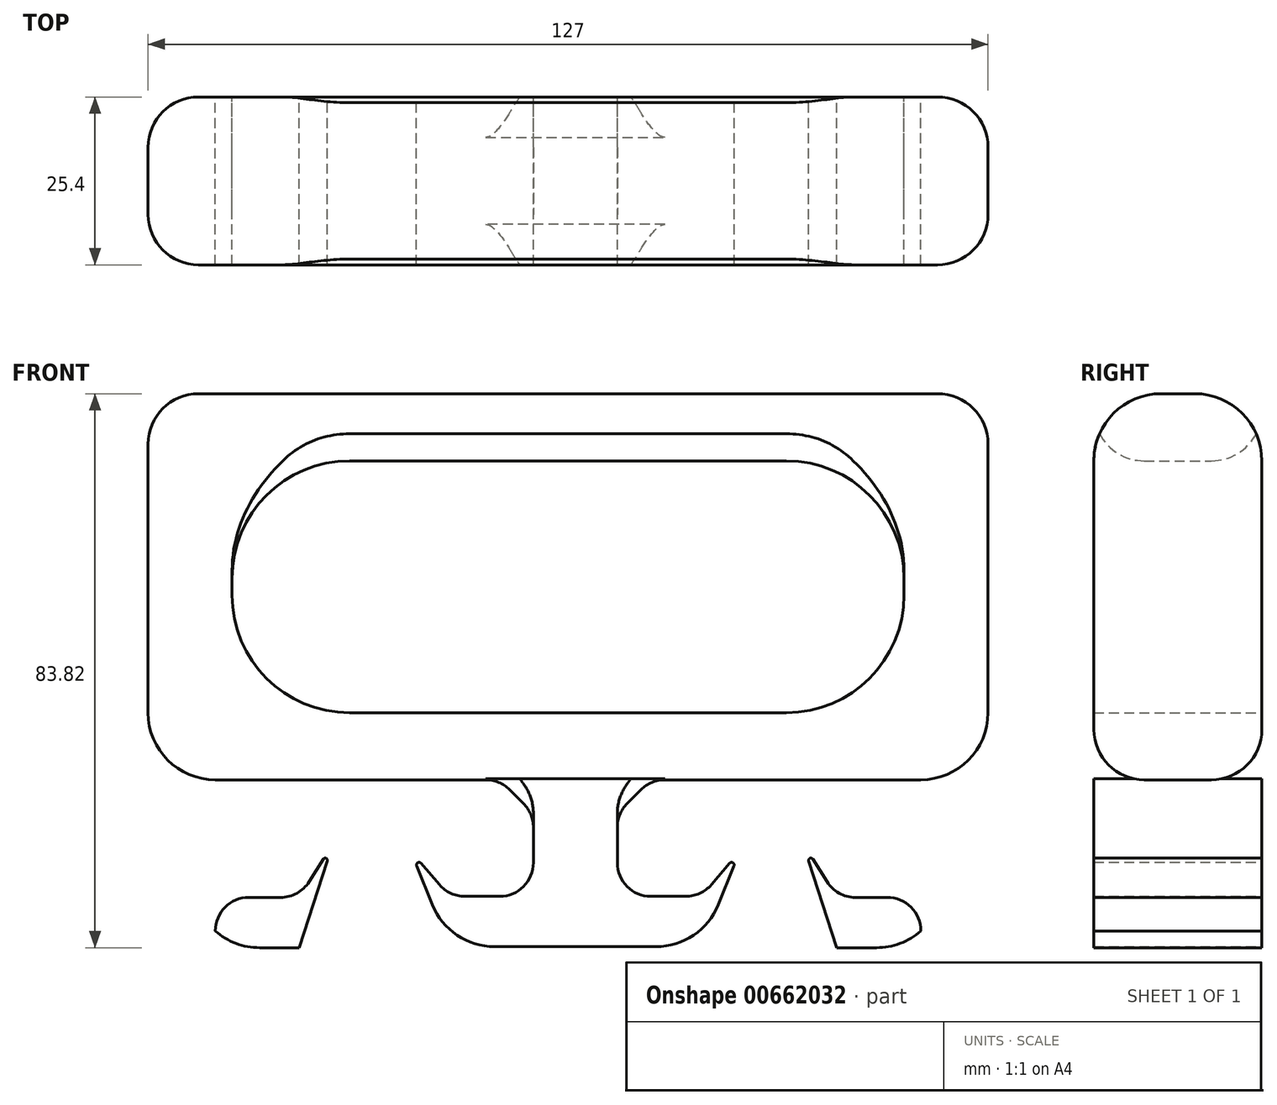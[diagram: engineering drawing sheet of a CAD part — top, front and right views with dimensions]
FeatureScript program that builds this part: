
annotation { "Feature Type Name" : "Feature", "Feature Type Description" : "" }
export const myFeature = defineFeature(function(context is Context, id is Id, definition is map)
    precondition{}
    {
        {
            var Q0;
            Q0=qCreatedBy(makeId("Front.planeOp"),FACE);
            var sketch = newSketch(context, id + "F0", { "sketchPlane" : qUnion([Q0])});
            skLineSegment(sketch, "E0.bottom", {"start": v(-50.8, 19.05) * mm, "end": v(50.8, 19.05) * mm});
            skLineSegment(sketch, "E0.top", {"start": v(-50.8, -19.05) * mm, "end": v(50.8, -19.05) * mm});
            skLineSegment(sketch, "E0.left", {"start": v(-50.8, 19.05) * mm, "end": v(-50.8, -19.05) * mm});
            skLineSegment(sketch, "E0.right", {"start": v(50.8, 19.05) * mm, "end": v(50.8, -19.05) * mm});
            skPoint(sketch, "E0.middle", {"position": v(0, 0) * mm});
            skLineSegment(sketch, "E1.bottom", {"start": v(-63.5, 29.21) * mm, "end": v(63.5, 29.21) * mm});
            skLineSegment(sketch, "E1.top", {"start": v(-63.5, -29.21) * mm, "end": v(63.5, -29.21) * mm});
            skLineSegment(sketch, "E1.left", {"start": v(-63.5, 29.21) * mm, "end": v(-63.5, -29.21) * mm});
            skLineSegment(sketch, "E1.right", {"start": v(63.5, 29.21) * mm, "end": v(63.5, -29.21) * mm});
            skPoint(sketch, "E2.endSnap0", {"position": v(0, -29.21) * mm});
            skLineSegment(sketch, "E3", {"start": v(0, -54.61) * mm, "end": v(0, -41.91) * mm});
            skLineSegment(sketch, "E4.bottom", {"start": v(-5.08, -54.61) * mm, "end": v(5.08, -54.61) * mm});
            skLineSegment(sketch, "E4.top", {"start": v(-5.08, -29.2) * mm, "end": v(5.08, -29.2) * mm});
            skLineSegment(sketch, "E4.left", {"start": v(-5.08, -54.61) * mm, "end": v(-5.08, -29.2) * mm});
            skLineSegment(sketch, "E4.right", {"start": v(5.08, -54.61) * mm, "end": v(5.08, -29.2) * mm});
            skPoint(sketch, "E4.middle", {"position": v(0, -41.91) * mm});
            skLineSegment(sketch, "E5.bottom", {"start": v(-63.5, -29.21) * mm, "end": v(-53.34, -29.21) * mm});
            skLineSegment(sketch, "E5.top", {"start": v(-63.5, -54.61) * mm, "end": v(-53.34, -54.61) * mm});
            skLineSegment(sketch, "E5.left", {"start": v(-63.5, -29.21) * mm, "end": v(-63.5, -54.61) * mm});
            skLineSegment(sketch, "E5.right", {"start": v(-53.34, -29.21) * mm, "end": v(-53.34, -54.61) * mm});
            skLineSegment(sketch, "E6.bottom", {"start": v(63.5, -29.21) * mm, "end": v(53.34, -29.21) * mm});
            skLineSegment(sketch, "E6.top", {"start": v(63.5, -54.6) * mm, "end": v(53.34, -54.6) * mm});
            skLineSegment(sketch, "E6.left", {"start": v(63.5, -29.21) * mm, "end": v(63.5, -54.6) * mm});
            skLineSegment(sketch, "E6.right", {"start": v(53.34, -29.2) * mm, "end": v(53.34, -54.6) * mm});
            skLineSegment(sketch, "E7.bottom", {"start": v(-53.34, -54.61) * mm, "end": v(-40.64, -54.61) * mm});
            skLineSegment(sketch, "E7.top", {"start": v(-53.34, -47) * mm, "end": v(-40.64, -47) * mm});
            skLineSegment(sketch, "E7.left", {"start": v(-53.34, -54.61) * mm, "end": v(-53.34, -47) * mm});
            skLineSegment(sketch, "E7.right", {"start": v(-40.64, -54.61) * mm, "end": v(-40.64, -47) * mm});
            skLineSegment(sketch, "E8.bottom", {"start": v(-5.08, -54.61) * mm, "end": v(-17.78, -54.61) * mm});
            skLineSegment(sketch, "E8.top", {"start": v(-5.08, -47) * mm, "end": v(-17.78, -47) * mm});
            skLineSegment(sketch, "E8.left", {"start": v(-5.08, -54.61) * mm, "end": v(-5.08, -47) * mm});
            skLineSegment(sketch, "E8.right", {"start": v(-17.78, -54.61) * mm, "end": v(-17.78, -47) * mm});
            skLineSegment(sketch, "E9.bottom", {"start": v(5.08, -54.61) * mm, "end": v(17.78, -54.61) * mm});
            skLineSegment(sketch, "E9.top", {"start": v(5.08, -47) * mm, "end": v(17.78, -47) * mm});
            skLineSegment(sketch, "E9.left", {"start": v(5.08, -54.61) * mm, "end": v(5.08, -47) * mm});
            skLineSegment(sketch, "E9.right", {"start": v(17.78, -54.61) * mm, "end": v(17.78, -47) * mm});
            skLineSegment(sketch, "E10.bottom", {"start": v(53.34, -54.6) * mm, "end": v(40.64, -54.6) * mm});
            skLineSegment(sketch, "E10.top", {"start": v(53.34, -47) * mm, "end": v(40.64, -47) * mm});
            skLineSegment(sketch, "E10.left", {"start": v(53.34, -54.6) * mm, "end": v(53.34, -47) * mm});
            skLineSegment(sketch, "E10.right", {"start": v(40.64, -54.6) * mm, "end": v(40.64, -47) * mm});
            skLineSegment(sketch, "E11", {"start": v(-40.64, -54.61) * mm, "end": v(-35.59, -38.97) * mm});
            skLineSegment(sketch, "E12", {"start": v(-35.59, -38.97) * mm, "end": v(-40.64, -47) * mm});
            skLineSegment(sketch, "E13", {"start": v(-17.78, -54.61) * mm, "end": v(-22.84, -38.98) * mm});
            skLineSegment(sketch, "E14", {"start": v(-22.84, -38.98) * mm, "end": v(-17.78, -47) * mm});
            skLineSegment(sketch, "E15", {"start": v(17.78, -47) * mm, "end": v(22.84, -38.98) * mm});
            skLineSegment(sketch, "E16", {"start": v(22.84, -38.98) * mm, "end": v(17.78, -54.61) * mm});
            skLineSegment(sketch, "E17", {"start": v(40.64, -47) * mm, "end": v(35.59, -38.97) * mm});
            skLineSegment(sketch, "E18", {"start": v(35.59, -38.97) * mm, "end": v(40.64, -54.61) * mm});
            skSolve(sketch);
        }
        {
            var Q0;
            Q0=makeQuery(id+"F0.imprint","IMPRINT",FACE,{"disambiguationData":[TD([[makeQuery(id+"F0.imprint","IMPRINT",EDGE,{"derivedFrom":sQuery(id+"F0.wireOp",EDGE,"E0.bottom")}),1.0]])]});
            var Q1;
            Q1=makeQuery(id+"F0.imprint","IMPRINT",FACE,{"disambiguationData":[TD([[makeQuery(id+"F0.imprint","IMPRINT",EDGE,{"derivedFrom":sQuery(id+"F0.wireOp",EDGE,"E6.bottom")}),1.0]])]});
            var Q2;
            Q2=makeQuery(id+"F0.imprint","IMPRINT",FACE,{"disambiguationData":[TD([[makeQuery(id+"F0.imprint","IMPRINT",EDGE,{"derivedFrom":sQuery(id+"F0.wireOp",EDGE,"E10.bottom")}),-1.0]])]});
            var Q3;
            Q3=makeQuery(id+"F0.imprint","IMPRINT",FACE,{"disambiguationData":[TD([[makeQuery(id+"F0.imprint","IMPRINT",EDGE,{"derivedFrom":sQuery(id+"F0.wireOp",EDGE,"E10.right")}),1.0]])]});
            var Q4;
            Q4=makeQuery(id+"F0.imprint","IMPRINT",FACE,{"disambiguationData":[TD([[makeQuery(id+"F0.imprint","IMPRINT",EDGE,{"derivedFrom":sQuery(id+"F0.wireOp",EDGE,"E5.bottom")}),-1.0]])]});
            var Q5;
            Q5=makeQuery(id+"F0.imprint","IMPRINT",FACE,{"disambiguationData":[TD([[makeQuery(id+"F0.imprint","IMPRINT",EDGE,{"derivedFrom":sQuery(id+"F0.wireOp",EDGE,"E7.bottom")}),1.0]])]});
            var Q6;
            Q6=makeQuery(id+"F0.imprint","IMPRINT",FACE,{"disambiguationData":[TD([[makeQuery(id+"F0.imprint","IMPRINT",EDGE,{"derivedFrom":sQuery(id+"F0.wireOp",EDGE,"E7.right")}),-1.0]])]});
            extrude(context, id + "F1", {"entities" : qUnion([Q0, Q1, Q2, Q3, Q4, Q5, Q6]), "depth" : 25.4 * mm, "offsetDistance" : 25.4 * mm});
        }
        {
            var Q0;
            Q0=makeQuery(id+"FVxEdmfXCbVZqXA_0.opExtrude","SWEPT_EDGE",EDGE,{"disambiguationData":[OSD([sQuery(id+"F0.wireOp",EDGE,"E13"),sQuery(id+"F0.wireOp",EDGE,"E14")])]});
            var Q1;
            Q1=makeQuery(id+"F1.opExtrude","SWEPT_EDGE",EDGE,{"disambiguationData":[OSD([sQuery(id+"F0.wireOp",EDGE,"E11"),sQuery(id+"F0.wireOp",EDGE,"E12")])]});
            var Q2;
            Q2=makeQuery(id+"FVxEdmfXCbVZqXA_0.opExtrude","SWEPT_EDGE",EDGE,{"disambiguationData":[OSD([sQuery(id+"F0.wireOp",EDGE,"E15"),sQuery(id+"F0.wireOp",EDGE,"E16")])]});
            var Q3;
            Q3=makeQuery(id+"F1.opExtrude","SWEPT_EDGE",EDGE,{"disambiguationData":[OSD([sQuery(id+"F0.wireOp",EDGE,"E17"),sQuery(id+"F0.wireOp",EDGE,"E18")])]});
            fillet(context, id + "F2", {"entities" : qUnion([Q0, Q1, Q2, Q3]), "radius" : 0.33 * mm, "tangentPropagation" : true, "allowEdgeOverflow" : false});
        }
        {
            var Q0;
            Q0=makeQuery(id+"FVxEdmfXCbVZqXA_0.opExtrude","SWEPT_EDGE",EDGE,{"disambiguationData":[OSD([sQuery(id+"F0.wireOp",EDGE,"E4.right"),sQuery(id+"F0.wireOp",EDGE,"E9.top"),sQuery(id+"F0.wireOp",EDGE,"E9.left")])]});
            var Q1;
            Q1=makeQuery(id+"FVxEdmfXCbVZqXA_0.opExtrude","SWEPT_EDGE",EDGE,{"disambiguationData":[OSD([sQuery(id+"F0.wireOp",EDGE,"E4.left"),sQuery(id+"F0.wireOp",EDGE,"E8.top"),sQuery(id+"F0.wireOp",EDGE,"E8.left")])]});
            var Q2;
            Q2=makeQuery(id+"F1.opExtrude","SWEPT_EDGE",EDGE,{"disambiguationData":[OSD([sQuery(id+"F0.wireOp",EDGE,"E6.right"),sQuery(id+"F0.wireOp",EDGE,"E10.top"),sQuery(id+"F0.wireOp",EDGE,"E10.left")])]});
            var Q3;
            Q3=makeQuery(id+"F1.opExtrude","SWEPT_EDGE",EDGE,{"disambiguationData":[OSD([sQuery(id+"F0.wireOp",EDGE,"E5.right"),sQuery(id+"F0.wireOp",EDGE,"E7.top"),sQuery(id+"F0.wireOp",EDGE,"E7.left")])]});
            fillet(context, id + "F3", {"entities" : qUnion([Q0, Q1, Q2, Q3]), "radius" : 5.08 * mm, "tangentPropagation" : true, "allowEdgeOverflow" : false});
        }
        {
            var Q0;
            Q0=makeQuery(id+"F1.opExtrude","SWEPT_EDGE",EDGE,{"disambiguationData":[OSD([sQuery(id+"F0.wireOp",EDGE,"E7.top"),sQuery(id+"F0.wireOp",EDGE,"E7.right"),sQuery(id+"F0.wireOp",EDGE,"E12")])]});
            var Q1;
            Q1=makeQuery(id+"FVxEdmfXCbVZqXA_0.opExtrude","SWEPT_EDGE",EDGE,{"disambiguationData":[OSD([sQuery(id+"F0.wireOp",EDGE,"E8.top"),sQuery(id+"F0.wireOp",EDGE,"E8.right"),sQuery(id+"F0.wireOp",EDGE,"E14")])]});
            var Q2;
            Q2=makeQuery(id+"FVxEdmfXCbVZqXA_0.opExtrude","SWEPT_EDGE",EDGE,{"disambiguationData":[OSD([sQuery(id+"F0.wireOp",EDGE,"E9.top"),sQuery(id+"F0.wireOp",EDGE,"E9.right"),sQuery(id+"F0.wireOp",EDGE,"E15")])]});
            var Q3;
            Q3=makeQuery(id+"F1.opExtrude","SWEPT_EDGE",EDGE,{"disambiguationData":[OSD([sQuery(id+"F0.wireOp",EDGE,"E10.top"),sQuery(id+"F0.wireOp",EDGE,"E10.right"),sQuery(id+"F0.wireOp",EDGE,"E17")])]});
            fillet(context, id + "F4", {"entities" : qUnion([Q0, Q1, Q2, Q3]), "radius" : 5.08 * mm, "tangentPropagation" : true, "allowEdgeOverflow" : false});
        }
        {
            var Q0;
            Q0=makeQuery(id+"FVxEdmfXCbVZqXA_0.opExtrude","SWEPT_EDGE",EDGE,{"disambiguationData":[OSD([sQuery(id+"F0.wireOp",EDGE,"E8.bottom"),sQuery(id+"F0.wireOp",EDGE,"E8.right"),sQuery(id+"F0.wireOp",EDGE,"E13")])]});
            var Q1;
            Q1=makeQuery(id+"FVxEdmfXCbVZqXA_0.opExtrude","SWEPT_EDGE",EDGE,{"disambiguationData":[OSD([sQuery(id+"F0.wireOp",EDGE,"E9.bottom"),sQuery(id+"F0.wireOp",EDGE,"E9.right"),sQuery(id+"F0.wireOp",EDGE,"E16")])]});
            var Q2;
            Q2=makeQuery(id+"F1.opExtrude","SWEPT_EDGE",EDGE,{"disambiguationData":[OSD([sQuery(id+"F0.wireOp",EDGE,"E5.top"),sQuery(id+"F0.wireOp",EDGE,"E5.left")])]});
            var Q3;
            Q3=makeQuery(id+"F1.opExtrude","SWEPT_EDGE",EDGE,{"disambiguationData":[OSD([sQuery(id+"F0.wireOp",EDGE,"E6.top"),sQuery(id+"F0.wireOp",EDGE,"E6.left")])]});
            fillet(context, id + "F5", {"entities" : qUnion([Q0, Q1, Q2, Q3]), "radius" : 10.16 * mm, "tangentPropagation" : true, "allowEdgeOverflow" : false});
        }
        {
            var Q0;
            Q0=makeQuery(id+"F1.opExtrude","CAP_EDGE",EDGE,{"disambiguationData":[OSD([sQuery(id+"F0.wireOp",EDGE,"E0.bottom")])],"isStart":true});
            var Q1;
            Q1=makeQuery(id+"F1.opExtrude","CAP_EDGE",EDGE,{"disambiguationData":[OSD([sQuery(id+"F0.wireOp",EDGE,"E0.bottom")])],"isStart":false});
            fillet(context, id + "F6", {"entities" : qUnion([Q0, Q1]), "radius" : 7.62 * mm, "tangentPropagation" : true, "allowEdgeOverflow" : false});
        }
        {
            var Q0;
            Q0=makeQuery(id+"F1.opExtrude","CAP_EDGE",EDGE,{"disambiguationData":[OSD([sQuery(id+"F0.wireOp",EDGE,"E1.bottom")])],"isStart":true});
            var Q1;
            Q1=makeQuery(id+"F1.opExtrude","CAP_EDGE",EDGE,{"disambiguationData":[OSD([sQuery(id+"F0.wireOp",EDGE,"E1.bottom")])],"isStart":false});
            fillet(context, id + "F7", {"entities" : qUnion([Q0, Q1]), "radius" : 10.16 * mm, "tangentPropagation" : true, "allowEdgeOverflow" : false});
        }
        {
            var Q0;
            Q0=makeQuery(id+"F1.opExtrude","CAP_EDGE",EDGE,{"disambiguationData":[OSD([sQuery(id+"F0.wireOp",EDGE,"E1.left"),sQuery(id+"F0.wireOp",EDGE,"E5.left")])],"isStart":false});
            var Q1;
            Q1=makeQuery(id+"F1.opExtrude","CAP_EDGE",EDGE,{"disambiguationData":[OSD([sQuery(id+"F0.wireOp",EDGE,"E1.left"),sQuery(id+"F0.wireOp",EDGE,"E5.left")])],"isStart":true});
            var Q2;
            Q2=makeQuery(id+"F1.opExtrude","CAP_EDGE",EDGE,{"disambiguationData":[OSD([sQuery(id+"F0.wireOp",EDGE,"E1.right"),sQuery(id+"F0.wireOp",EDGE,"E6.left")])],"isStart":true});
            var Q3;
            Q3=makeQuery(id+"F1.opExtrude","CAP_EDGE",EDGE,{"disambiguationData":[OSD([sQuery(id+"F0.wireOp",EDGE,"E1.right"),sQuery(id+"F0.wireOp",EDGE,"E6.left")])],"isStart":false});
            fillet(context, id + "F8", {"entities" : qUnion([Q0, Q1, Q2, Q3]), "radius" : 7.62 * mm, "tangentPropagation" : true, "allowEdgeOverflow" : false});
        }
        {
            var Q0;
            Q0=qCreatedBy(makeId("Front.planeOp"),FACE);
            var sketch = newSketch(context, id + "F9", { "sketchPlane" : qUnion([Q0])});
            skLineSegment(sketch, "E19.bottom", {"start": v(-5.25, -29.06) * mm, "end": v(7.45, -29.06) * mm});
            skLineSegment(sketch, "E19.top", {"start": v(-7.45, 29.06) * mm, "end": v(5.25, 29.06) * mm});
            skPoint(sketch, "E19.middle", {"position": v(0, 0) * mm});
            skLineSegment(sketch, "E20.0", {"start": v(5.08, -29.21) * mm, "end": v(53.34, -29.21) * mm});
            skLineSegment(sketch, "E21.top", {"start": v(-5.25, -54.46) * mm, "end": v(7.45, -54.46) * mm});
            skLineSegment(sketch, "E21.left", {"start": v(-5.25, -29.06) * mm, "end": v(-5.25, -54.46) * mm});
            skLineSegment(sketch, "E21.right", {"start": v(7.45, -29.06) * mm, "end": v(7.45, -54.46) * mm});
            skLineSegment(sketch, "E22.bottom", {"start": v(-5.25, -54.46) * mm, "end": v(-17.95, -54.46) * mm});
            skLineSegment(sketch, "E22.top", {"start": v(-5.25, -46.84) * mm, "end": v(-17.95, -46.84) * mm});
            skLineSegment(sketch, "E22.left", {"start": v(-5.25, -54.46) * mm, "end": v(-5.25, -46.84) * mm});
            skLineSegment(sketch, "E22.right", {"start": v(-17.95, -54.46) * mm, "end": v(-17.95, -46.84) * mm});
            skLineSegment(sketch, "E23.bottom", {"start": v(7.45, -54.46) * mm, "end": v(20.15, -54.46) * mm});
            skLineSegment(sketch, "E23.top", {"start": v(7.45, -46.84) * mm, "end": v(20.15, -46.84) * mm});
            skLineSegment(sketch, "E23.left", {"start": v(7.45, -54.46) * mm, "end": v(7.45, -46.84) * mm});
            skLineSegment(sketch, "E23.right", {"start": v(20.15, -54.46) * mm, "end": v(20.15, -46.84) * mm});
            skLineSegment(sketch, "E24", {"start": v(-17.95, -54.46) * mm, "end": v(-23.75, -40.07) * mm});
            skLineSegment(sketch, "E25", {"start": v(-23.75, -40.07) * mm, "end": v(-17.95, -46.84) * mm});
            skLineSegment(sketch, "E26", {"start": v(20.15, -46.84) * mm, "end": v(25.96, -40.07) * mm});
            skLineSegment(sketch, "E27", {"start": v(25.96, -40.07) * mm, "end": v(20.15, -54.46) * mm});
            skSolve(sketch);
        }
        {
            var Q0;
            Q0=qSketchRegion(id+"F9",true);
            extrude(context, id + "F10", {"entities" : qUnion([Q0]), "operationType" : NewBodyOperationType.ADD, "depth" : 25.4 * mm, "offsetDistance" : 25.4 * mm});
        }
        {
            var Q0;
            Q0=makeQuery(id+"F10.opExtrude","SWEPT_EDGE",EDGE,{"disambiguationData":[OSD([sQuery(id+"F9.wireOp",EDGE,"E24"),sQuery(id+"F9.wireOp",EDGE,"E25")])]});
            var Q1;
            Q1=makeQuery(id+"F10.opExtrude","SWEPT_EDGE",EDGE,{"disambiguationData":[OSD([sQuery(id+"F9.wireOp",EDGE,"E26"),sQuery(id+"F9.wireOp",EDGE,"E27")])]});
            fillet(context, id + "F11", {"entities" : qUnion([Q0, Q1]), "radius" : 0.38 * mm, "tangentPropagation" : true, "allowEdgeOverflow" : false});
        }
        {
            var Q0;
            Q0=makeQuery(id+"F10.opExtrude","SWEPT_EDGE",EDGE,{"disambiguationData":[OSD([sQuery(id+"F9.wireOp",EDGE,"E21.left"),sQuery(id+"F9.wireOp",EDGE,"E22.top"),sQuery(id+"F9.wireOp",EDGE,"E22.left")])]});
            var Q1;
            Q1=makeQuery(id+"F10.opExtrude","SWEPT_EDGE",EDGE,{"disambiguationData":[OSD([sQuery(id+"F9.wireOp",EDGE,"E21.right"),sQuery(id+"F9.wireOp",EDGE,"E23.top"),sQuery(id+"F9.wireOp",EDGE,"E23.left")])]});
            var Q2;
            Q2=makeQuery(id+"F10.opExtrude","SWEPT_EDGE",EDGE,{"disambiguationData":[OSD([sQuery(id+"F9.wireOp",EDGE,"E23.top"),sQuery(id+"F9.wireOp",EDGE,"E23.right"),sQuery(id+"F9.wireOp",EDGE,"E26")])]});
            var Q3;
            Q3=makeQuery(id+"F10.opExtrude","SWEPT_EDGE",EDGE,{"disambiguationData":[OSD([sQuery(id+"F9.wireOp",EDGE,"E22.top"),sQuery(id+"F9.wireOp",EDGE,"E22.right"),sQuery(id+"F9.wireOp",EDGE,"E25")])]});
            fillet(context, id + "F12", {"entities" : qUnion([Q0, Q1, Q2, Q3]), "radius" : 5.08 * mm, "tangentPropagation" : true, "allowEdgeOverflow" : false});
        }
        {
            var Q0;
            {var subQ0=sQuery(id+"F0.wireOp",EDGE,"E1.top");Q0=makeQuery(id+"F10.boolean.opBoolean","INTERSECT",EDGE,{"derivedFrom":[makeQuery(id+"F1.opExtrude","SWEPT_FACE",FACE,{"disambiguationData":[OSD([subQ0]),TDD([makeQuery(id+"F0.imprint","IMPRINT",EDGE,{"disambiguationData":[TD([[makeQuery(id+"F0.imprint","INTERSECT",VERTEX,{"derivedFrom":[subQ0,sQuery(id+"F0.wireOp",EDGE,"E4.right")]}),-1.0]])],"derivedFrom":subQ0})])]}),makeQuery(id+"F10.opExtrude","SWEPT_FACE",FACE,{"disambiguationData":[OSD([sQuery(id+"F9.wireOp",EDGE,"E21.right")])]})]});}
            var Q1;
            {var subQ0=sQuery(id+"F0.wireOp",EDGE,"E1.top");Q1=makeQuery(id+"F10.boolean.opBoolean","INTERSECT",EDGE,{"derivedFrom":[makeQuery(id+"F1.opExtrude","SWEPT_FACE",FACE,{"disambiguationData":[OSD([subQ0]),TDD([makeQuery(id+"F0.imprint","IMPRINT",EDGE,{"disambiguationData":[TD([[makeQuery(id+"F0.imprint","INTERSECT",VERTEX,{"derivedFrom":[subQ0,sQuery(id+"F0.wireOp",EDGE,"E4.left")]}),1.0]])],"derivedFrom":subQ0})])]}),makeQuery(id+"F10.opExtrude","SWEPT_FACE",FACE,{"disambiguationData":[OSD([sQuery(id+"F9.wireOp",EDGE,"E21.left")])]})]});}
            var Q2;
            Q2=makeQuery(id+"F1.opExtrude","SWEPT_EDGE",EDGE,{"disambiguationData":[OSD([sQuery(id+"F0.wireOp",EDGE,"E1.top"),sQuery(id+"F0.wireOp",EDGE,"E6.bottom"),sQuery(id+"F0.wireOp",EDGE,"E6.right")])]});
            var Q3;
            Q3=makeQuery(id+"F1.opExtrude","SWEPT_EDGE",EDGE,{"disambiguationData":[OSD([sQuery(id+"F0.wireOp",EDGE,"E1.top"),sQuery(id+"F0.wireOp",EDGE,"E5.bottom"),sQuery(id+"F0.wireOp",EDGE,"E5.right")])]});
            chamfer(context, id + "F13", {"entities" : qUnion([Q0, Q1, Q2, Q3]), "width" : 5.08 * mm, "tangentPropagation" : true});
        }
        {
            var Q0;
            {var subQ0=sQuery(id+"F0.wireOp",EDGE,"E5.right");Q0=makeQuery(id+"F13.opChamfer","BLEND_EDGE",EDGE,{"blendedFrom":[makeQuery(id+"F1.opExtrude","SWEPT_EDGE",EDGE,{"disambiguationData":[OSD([sQuery(id+"F0.wireOp",EDGE,"E1.top"),sQuery(id+"F0.wireOp",EDGE,"E5.bottom"),subQ0])]}),makeQuery(id+"F1.opExtrude","SWEPT_FACE",FACE,{"disambiguationData":[OSD([subQ0])]})],"blendedInto":[makeQuery(id+"F1.opExtrude","SWEPT_FACE",FACE,{"disambiguationData":[OSD([subQ0])]})]});}
            var Q1;
            {var subQ0=sQuery(id+"F0.wireOp",EDGE,"E5.right");var subQ1=sQuery(id+"F0.wireOp",EDGE,"E5.bottom");var subQ2=sQuery(id+"F0.wireOp",EDGE,"E1.top");Q1=makeQuery(id+"F13.opChamfer","BLEND_EDGE",EDGE,{"blendedFrom":[makeQuery(id+"F1.opExtrude","SWEPT_EDGE",EDGE,{"disambiguationData":[OSD([subQ2,subQ1,subQ0])]}),makeQuery(id+"F1.opExtrude","SWEPT_FACE",FACE,{"disambiguationData":[OSD([subQ2]),TDD([makeQuery(id+"F0.imprint","IMPRINT",EDGE,{"disambiguationData":[TD([[makeQuery(id+"F0.imprint","INTERSECT",VERTEX,{"derivedFrom":[subQ2,sQuery(id+"F0.wireOp",EDGE,"E4.left")]}),1.0]])],"derivedFrom":subQ2})])]})],"blendedInto":[makeQuery(id+"F1.opExtrude","SWEPT_FACE",FACE,{"disambiguationData":[OSD([subQ2]),TDD([makeQuery(id+"F0.imprint","IMPRINT",EDGE,{"disambiguationData":[TD([[makeQuery(id+"F0.imprint","INTERSECT",VERTEX,{"derivedFrom":[subQ2,sQuery(id+"F0.wireOp",EDGE,"E4.left")]}),1.0]])],"derivedFrom":subQ2})])]})]});}
            var Q2;
            {var subQ0=sQuery(id+"F0.wireOp",EDGE,"E1.top");var subQ1=makeQuery(id+"F1.opExtrude","SWEPT_FACE",FACE,{"disambiguationData":[OSD([subQ0]),TDD([makeQuery(id+"F0.imprint","IMPRINT",EDGE,{"disambiguationData":[TD([[makeQuery(id+"F0.imprint","INTERSECT",VERTEX,{"derivedFrom":[subQ0,sQuery(id+"F0.wireOp",EDGE,"E4.left")]}),1.0]])],"derivedFrom":subQ0})])]});Q2=makeQuery(id+"F13.opChamfer","BLEND_EDGE",EDGE,{"blendedFrom":[makeQuery(id+"F10.boolean.opBoolean","INTERSECT",EDGE,{"derivedFrom":[subQ1,makeQuery(id+"F10.opExtrude","SWEPT_FACE",FACE,{"disambiguationData":[OSD([sQuery(id+"F9.wireOp",EDGE,"E21.left")])]})]}),subQ1],"blendedInto":[subQ1]});}
            var Q3;
            {var subQ0=makeQuery(id+"F10.opExtrude","SWEPT_FACE",FACE,{"disambiguationData":[OSD([sQuery(id+"F9.wireOp",EDGE,"E21.left")])]});var subQ1=sQuery(id+"F0.wireOp",EDGE,"E1.top");Q3=makeQuery(id+"F13.opChamfer","BLEND_EDGE",EDGE,{"blendedFrom":[makeQuery(id+"F10.boolean.opBoolean","INTERSECT",EDGE,{"derivedFrom":[makeQuery(id+"F1.opExtrude","SWEPT_FACE",FACE,{"disambiguationData":[OSD([subQ1]),TDD([makeQuery(id+"F0.imprint","IMPRINT",EDGE,{"disambiguationData":[TD([[makeQuery(id+"F0.imprint","INTERSECT",VERTEX,{"derivedFrom":[subQ1,sQuery(id+"F0.wireOp",EDGE,"E4.left")]}),1.0]])],"derivedFrom":subQ1})])]}),subQ0]}),subQ0],"blendedInto":[subQ0]});}
            var Q4;
            {var subQ0=makeQuery(id+"F10.opExtrude","SWEPT_FACE",FACE,{"disambiguationData":[OSD([sQuery(id+"F9.wireOp",EDGE,"E21.right")])]});var subQ1=sQuery(id+"F0.wireOp",EDGE,"E1.top");Q4=makeQuery(id+"F13.opChamfer","BLEND_EDGE",EDGE,{"blendedFrom":[makeQuery(id+"F10.boolean.opBoolean","INTERSECT",EDGE,{"derivedFrom":[makeQuery(id+"F1.opExtrude","SWEPT_FACE",FACE,{"disambiguationData":[OSD([subQ1]),TDD([makeQuery(id+"F0.imprint","IMPRINT",EDGE,{"disambiguationData":[TD([[makeQuery(id+"F0.imprint","INTERSECT",VERTEX,{"derivedFrom":[subQ1,sQuery(id+"F0.wireOp",EDGE,"E4.right")]}),-1.0]])],"derivedFrom":subQ1})])]}),subQ0]}),subQ0],"blendedInto":[subQ0]});}
            var Q5;
            {var subQ0=sQuery(id+"F0.wireOp",EDGE,"E1.top");var subQ1=makeQuery(id+"F1.opExtrude","SWEPT_FACE",FACE,{"disambiguationData":[OSD([subQ0]),TDD([makeQuery(id+"F0.imprint","IMPRINT",EDGE,{"disambiguationData":[TD([[makeQuery(id+"F0.imprint","INTERSECT",VERTEX,{"derivedFrom":[subQ0,sQuery(id+"F0.wireOp",EDGE,"E4.right")]}),-1.0]])],"derivedFrom":subQ0})])]});Q5=makeQuery(id+"F13.opChamfer","BLEND_EDGE",EDGE,{"blendedFrom":[makeQuery(id+"F10.boolean.opBoolean","INTERSECT",EDGE,{"derivedFrom":[subQ1,makeQuery(id+"F10.opExtrude","SWEPT_FACE",FACE,{"disambiguationData":[OSD([sQuery(id+"F9.wireOp",EDGE,"E21.right")])]})]}),subQ1],"blendedInto":[subQ1]});}
            var Q6;
            {var subQ0=sQuery(id+"F0.wireOp",EDGE,"E6.right");var subQ1=sQuery(id+"F0.wireOp",EDGE,"E6.bottom");var subQ2=sQuery(id+"F0.wireOp",EDGE,"E1.top");Q6=makeQuery(id+"F13.opChamfer","BLEND_EDGE",EDGE,{"blendedFrom":[makeQuery(id+"F1.opExtrude","SWEPT_EDGE",EDGE,{"disambiguationData":[OSD([subQ2,subQ1,subQ0])]}),makeQuery(id+"F1.opExtrude","SWEPT_FACE",FACE,{"disambiguationData":[OSD([subQ2]),TDD([makeQuery(id+"F0.imprint","IMPRINT",EDGE,{"disambiguationData":[TD([[makeQuery(id+"F0.imprint","INTERSECT",VERTEX,{"derivedFrom":[subQ2,sQuery(id+"F0.wireOp",EDGE,"E4.right")]}),-1.0]])],"derivedFrom":subQ2})])]})],"blendedInto":[makeQuery(id+"F1.opExtrude","SWEPT_FACE",FACE,{"disambiguationData":[OSD([subQ2]),TDD([makeQuery(id+"F0.imprint","IMPRINT",EDGE,{"disambiguationData":[TD([[makeQuery(id+"F0.imprint","INTERSECT",VERTEX,{"derivedFrom":[subQ2,sQuery(id+"F0.wireOp",EDGE,"E4.right")]}),-1.0]])],"derivedFrom":subQ2})])]})]});}
            var Q7;
            {var subQ0=sQuery(id+"F0.wireOp",EDGE,"E6.right");Q7=makeQuery(id+"F13.opChamfer","BLEND_EDGE",EDGE,{"blendedFrom":[makeQuery(id+"F1.opExtrude","SWEPT_EDGE",EDGE,{"disambiguationData":[OSD([sQuery(id+"F0.wireOp",EDGE,"E1.top"),sQuery(id+"F0.wireOp",EDGE,"E6.bottom"),subQ0])]}),makeQuery(id+"F1.opExtrude","SWEPT_FACE",FACE,{"disambiguationData":[OSD([subQ0])]})],"blendedInto":[makeQuery(id+"F1.opExtrude","SWEPT_FACE",FACE,{"disambiguationData":[OSD([subQ0])]})]});}
            fillet(context, id + "F14", {"entities" : qUnion([Q0, Q1, Q2, Q3, Q4, Q5, Q6, Q7]), "radius" : 5.08 * mm, "tangentPropagation" : true, "allowEdgeOverflow" : false});
        }
        {
            var Q0;
            Q0=makeQuery(id+"F1.opExtrude","SWEPT_EDGE",EDGE,{"disambiguationData":[OSD([sQuery(id+"F0.wireOp",EDGE,"E0.bottom"),sQuery(id+"F0.wireOp",EDGE,"E0.left")])]});
            var Q1;
            Q1=makeQuery(id+"F1.opExtrude","SWEPT_EDGE",EDGE,{"disambiguationData":[OSD([sQuery(id+"F0.wireOp",EDGE,"E0.bottom"),sQuery(id+"F0.wireOp",EDGE,"E0.right")])]});
            var Q2;
            Q2=makeQuery(id+"F1.opExtrude","SWEPT_EDGE",EDGE,{"disambiguationData":[OSD([sQuery(id+"F0.wireOp",EDGE,"E0.top"),sQuery(id+"F0.wireOp",EDGE,"E0.left")])]});
            var Q3;
            Q3=makeQuery(id+"F1.opExtrude","SWEPT_EDGE",EDGE,{"disambiguationData":[OSD([sQuery(id+"F0.wireOp",EDGE,"E0.top"),sQuery(id+"F0.wireOp",EDGE,"E0.right")])]});
            fillet(context, id + "F15", {"entities" : qUnion([Q0, Q1, Q2, Q3]), "radius" : 17.78 * mm, "tangentPropagation" : true, "allowEdgeOverflow" : false});
        }
        {
            var Q0;
            Q0=makeQuery(id+"F10.opExtrude","SWEPT_EDGE",EDGE,{"disambiguationData":[OSD([sQuery(id+"F9.wireOp",EDGE,"E22.bottom"),sQuery(id+"F9.wireOp",EDGE,"E22.right"),sQuery(id+"F9.wireOp",EDGE,"E24")])]});
            var Q1;
            Q1=makeQuery(id+"F10.opExtrude","SWEPT_EDGE",EDGE,{"disambiguationData":[OSD([sQuery(id+"F9.wireOp",EDGE,"E23.bottom"),sQuery(id+"F9.wireOp",EDGE,"E23.right"),sQuery(id+"F9.wireOp",EDGE,"E27")])]});
            fillet(context, id + "F16", {"entities" : qUnion([Q0, Q1]), "radius" : 10.16 * mm, "tangentPropagation" : true, "allowEdgeOverflow" : false});
        }
    });
